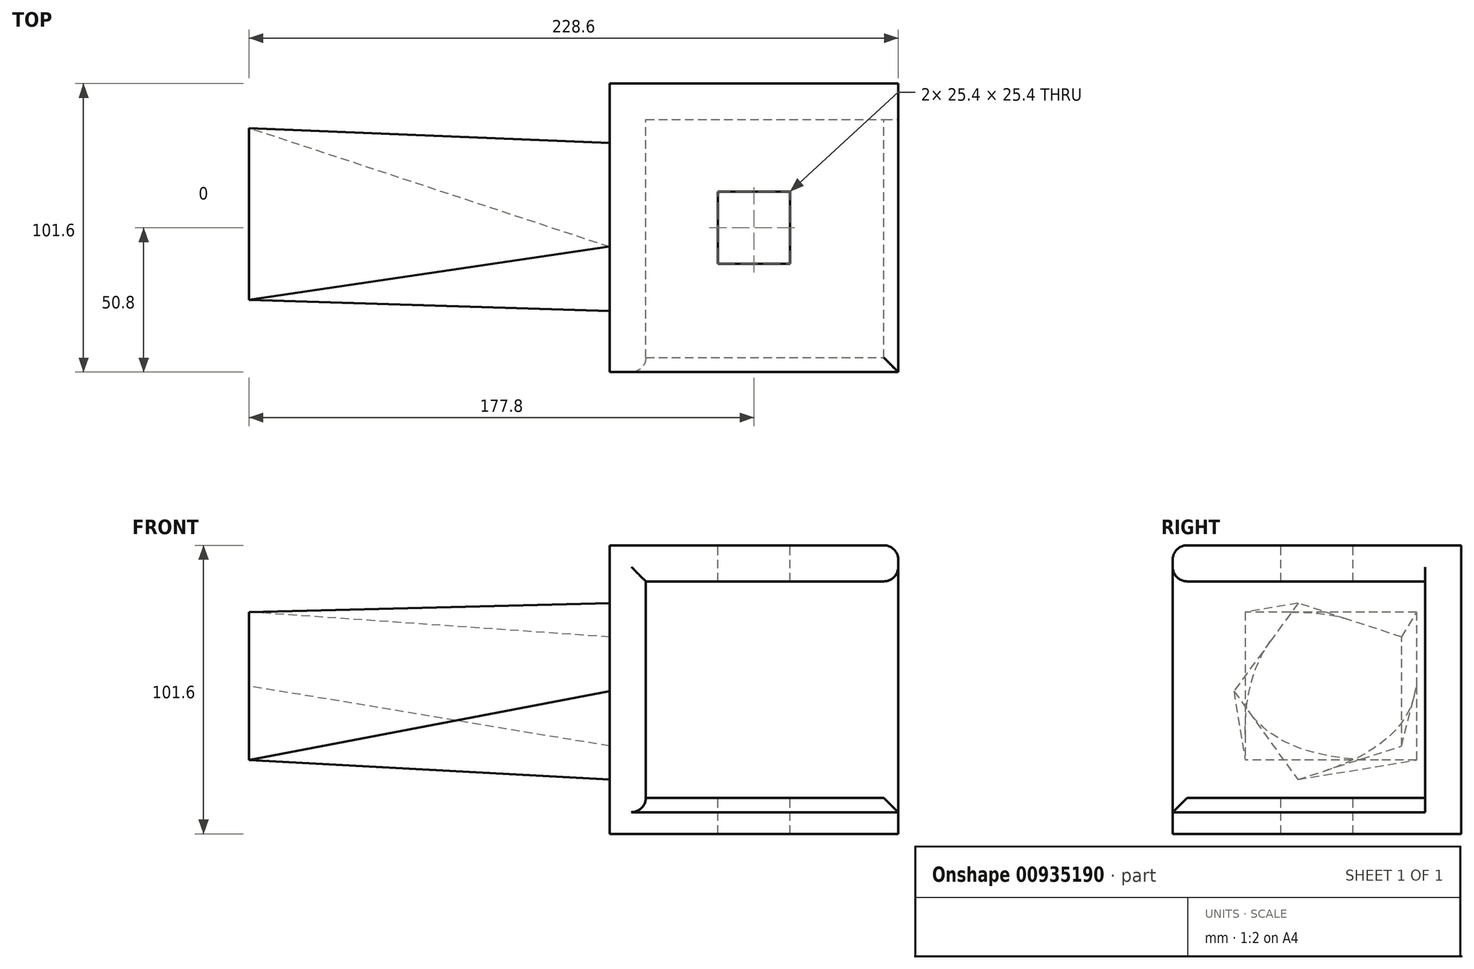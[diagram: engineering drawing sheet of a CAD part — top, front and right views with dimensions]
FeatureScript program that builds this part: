
annotation { "Feature Type Name" : "Feature", "Feature Type Description" : "" }
export const myFeature = defineFeature(function(context is Context, id is Id, definition is map)
    precondition{}
    {
        {
            var Q0;
            Q0=qCreatedBy(makeId("Front.planeOp"),FACE);
            var sketch = newSketch(context, id + "F0", { "sketchPlane" : qUnion([Q0])});
            skLineSegment(sketch, "E0.bottom", {"start": v(-101.6, -101.6) * mm, "end": v(0, -101.6) * mm});
            skLineSegment(sketch, "E0.top", {"start": v(-101.6, 0) * mm, "end": v(0, 0) * mm});
            skLineSegment(sketch, "E0.left", {"start": v(-101.6, -101.6) * mm, "end": v(-101.6, 0) * mm});
            skLineSegment(sketch, "E0.right", {"start": v(0, -101.6) * mm, "end": v(0, 0) * mm});
            skSolve(sketch);
        }
        {
            var Q0;
            Q0=makeQuery(id+"F0.imprint","IMPRINT",FACE,{"disambiguationData":[TD([[makeQuery(id+"F0.imprint","IMPRINT",EDGE,{"derivedFrom":sQuery(id+"F0.wireOp",EDGE,"E0.bottom")}),1.0]])]});
            extrude(context, id + "F1", {"entities" : qUnion([Q0]), "depth" : 101.6 * mm, "offsetDistance" : 25.4 * mm});
        }
        {
            var Q0;
            Q0=makeQuery(id+"F1.opExtrude","CAP_FACE",FACE,{"disambiguationData":[OSD([sQuery(id+"F0.wireOp",EDGE,"E0.bottom"),sQuery(id+"F0.wireOp",EDGE,"E0.top"),sQuery(id+"F0.wireOp",EDGE,"E0.left"),sQuery(id+"F0.wireOp",EDGE,"E0.right")])],"isStart":false});
            var Q1;
            Q1=makeQuery(id+"F1.opExtrude","SWEPT_FACE",FACE,{"disambiguationData":[OSD([sQuery(id+"F0.wireOp",EDGE,"E0.right")])]});
            shell(context, id + "F2", {"entities" : qUnion([Q0, Q1]), "thickness" : 12.7 * mm});
        }
        {
            var Q0;
            Q0=makeQuery(id+"F1.opExtrude","CAP_EDGE",EDGE,{"disambiguationData":[OSD([sQuery(id+"F0.wireOp",EDGE,"E0.top")])],"isStart":false});
            var Q1;
            Q1=makeQuery(id+"F1.opExtrude","SWEPT_EDGE",EDGE,{"disambiguationData":[OSD([sQuery(id+"F0.wireOp",EDGE,"E0.top"),sQuery(id+"F0.wireOp",EDGE,"E0.right")])]});
            var Q2;
            {var subQ0=sQuery(id+"F0.wireOp",EDGE,"E0.top");Q2=makeQuery(id+"F2.opShell","OFFSET_EDGE",EDGE,{"disambiguationData":[OSD([subQ0]),TDD([makeQuery(id+"F1.opExtrude","CAP_EDGE",EDGE,{"disambiguationData":[OSD([subQ0])],"isStart":false})])]});}
            var Q3;
            Q3=makeQuery(id+"F2.opShell","OFFSET_EDGE",EDGE,{"disambiguationData":[OSD([sQuery(id+"F0.wireOp",EDGE,"E0.top"),sQuery(id+"F0.wireOp",EDGE,"E0.right")])]});
            var Q4;
            {var subQ0=sQuery(id+"F0.wireOp",EDGE,"E0.left");Q4=makeQuery(id+"F2.opShell","OFFSET_EDGE",EDGE,{"disambiguationData":[OSD([subQ0]),TDD([makeQuery(id+"F1.opExtrude","CAP_EDGE",EDGE,{"disambiguationData":[OSD([subQ0])],"isStart":false})])]});}
            fillet(context, id + "F3", {"entities" : qUnion([Q0, Q1, Q2, Q3, Q4]), "radius" : 5.08 * mm, "tangentPropagation" : true, "allowEdgeOverflow" : false});
        }
        {
            var Q0;
            {var subQ0=sQuery(id+"F0.wireOp",EDGE,"E0.bottom");Q0=makeQuery(id+"F2.opShell","OFFSET_EDGE",EDGE,{"disambiguationData":[OSD([subQ0]),TDD([makeQuery(id+"F1.opExtrude","CAP_EDGE",EDGE,{"disambiguationData":[OSD([subQ0])],"isStart":false})])]});}
            var Q1;
            Q1=makeQuery(id+"F2.opShell","OFFSET_EDGE",EDGE,{"disambiguationData":[OSD([sQuery(id+"F0.wireOp",EDGE,"E0.bottom"),sQuery(id+"F0.wireOp",EDGE,"E0.right")])]});
            chamfer(context, id + "F4", {"entities" : qUnion([Q0, Q1]), "width" : 5.08 * mm, "tangentPropagation" : true});
        }
        {
            var Q0;
            Q0=makeQuery(id+"F2.opShell","OFFSET_FACE",FACE,{"disambiguationData":[OSD([sQuery(id+"F0.wireOp",EDGE,"E0.bottom")])]});
            var sketch = newSketch(context, id + "F5", { "sketchPlane" : qUnion([Q0])});
            skLineSegment(sketch, "E1.bottom", {"start": v(-63.5, -38.1) * mm, "end": v(-38.1, -38.1) * mm});
            skLineSegment(sketch, "E1.top", {"start": v(-63.5, -63.5) * mm, "end": v(-38.1, -63.5) * mm});
            skLineSegment(sketch, "E1.left", {"start": v(-63.5, -38.1) * mm, "end": v(-63.5, -63.5) * mm});
            skLineSegment(sketch, "E1.right", {"start": v(-38.1, -38.1) * mm, "end": v(-38.1, -63.5) * mm});
            skSolve(sketch);
        }
        {
            var Q0;
            Q0 = qSketchRegion(id + "F5", true);
            extrude(context, id + "F6", {"entities" : qUnion([Q0]), "operationType" : NewBodyOperationType.REMOVE, "oppositeDirection" : true, "depth" : 25.4 * mm, "offsetDistance" : 25.4 * mm, "hasSecondDirection" : true, "secondDirectionOppositeDirection" : false, "secondDirectionDepth" : 127 * mm});
        }
        {
            var Q0;
            Q0=makeQuery(id+"F1.opExtrude","SWEPT_FACE",FACE,{"disambiguationData":[OSD([sQuery(id+"F0.wireOp",EDGE,"E0.left")])]});
            var sketch = newSketch(context, id + "F7", { "sketchPlane" : qUnion([Q0])});
            skCircle(sketch, "E2.cCircle", {"center": v(47.4, -51.45) * mm, "radius": 26.42 * mm, "construction": true});
            skLineSegment(sketch, "E2.0", {"start": v(57.42, -20.36) * mm, "end": v(80.05, -51.38) * mm});
            skLineSegment(sketch, "E2.1", {"start": v(80.05, -51.38) * mm, "end": v(57.55, -82.48) * mm});
            skLineSegment(sketch, "E2.2", {"start": v(57.55, -82.48) * mm, "end": v(21.01, -70.7) * mm});
            skLineSegment(sketch, "E2.3", {"start": v(21.01, -70.7) * mm, "end": v(20.93, -32.3) * mm});
            skLineSegment(sketch, "E2.4", {"start": v(20.93, -32.3) * mm, "end": v(57.42, -20.36) * mm});
            skPoint(sketch, "E2.0.midPoint", {"position": v(68.73, -35.87) * mm});
            skSolve(sketch);
        }
        {
            var Q0;
            Q0=makeQuery(id+"F7.imprint","IMPRINT",FACE,{"disambiguationData":[TD([[makeQuery(id+"F7.imprint","IMPRINT",EDGE,{"derivedFrom":sQuery(id+"F7.wireOp",EDGE,"E2.0")}),1.0]])]});
            cPlane(context, id + "F8", {"entities" : qUnion([Q0]), "cplaneType" : CPlaneType.OFFSET, "offset" : 127 * mm, "width" : 152.4 * mm, "height" : 152.4 * mm});
        }
        {
            var Q0;
            Q0=qCreatedBy(id+"F8.planeOp",FACE);
            var sketch = newSketch(context, id + "F9", { "sketchPlane" : qUnion([Q0])});
            skLineSegment(sketch, "E3.bottom", {"start": v(15.69, -23.5) * mm, "end": v(76.11, -23.5) * mm});
            skLineSegment(sketch, "E3.top", {"start": v(15.69, -75.6) * mm, "end": v(76.11, -75.6) * mm});
            skLineSegment(sketch, "E3.left", {"start": v(15.69, -23.5) * mm, "end": v(15.69, -75.6) * mm});
            skLineSegment(sketch, "E3.right", {"start": v(76.11, -23.5) * mm, "end": v(76.11, -75.6) * mm});
            skSolve(sketch);
        }
        {
            var Q1;
            Q1=makeQuery(id+"F7.imprint","IMPRINT",FACE,{"disambiguationData":[TD([[makeQuery(id+"F7.imprint","IMPRINT",EDGE,{"derivedFrom":sQuery(id+"F7.wireOp",EDGE,"E2.0")}),-1.0]])]});
            var Q2;
            Q2=makeQuery(id+"F9.imprint","IMPRINT",FACE,{"disambiguationData":[TD([[makeQuery(id+"F9.imprint","IMPRINT",EDGE,{"derivedFrom":sQuery(id+"F9.wireOp",EDGE,"E3.bottom")}),-1.0]])]});
            loft(context, id + "F10", {"operationType" : NewBodyOperationType.ADD, "sheetProfilesArray" : [{ "sheetProfileEntities" : qUnion([Q1]) }, { "sheetProfileEntities" : qUnion([Q2]) }]});
        }
    });
